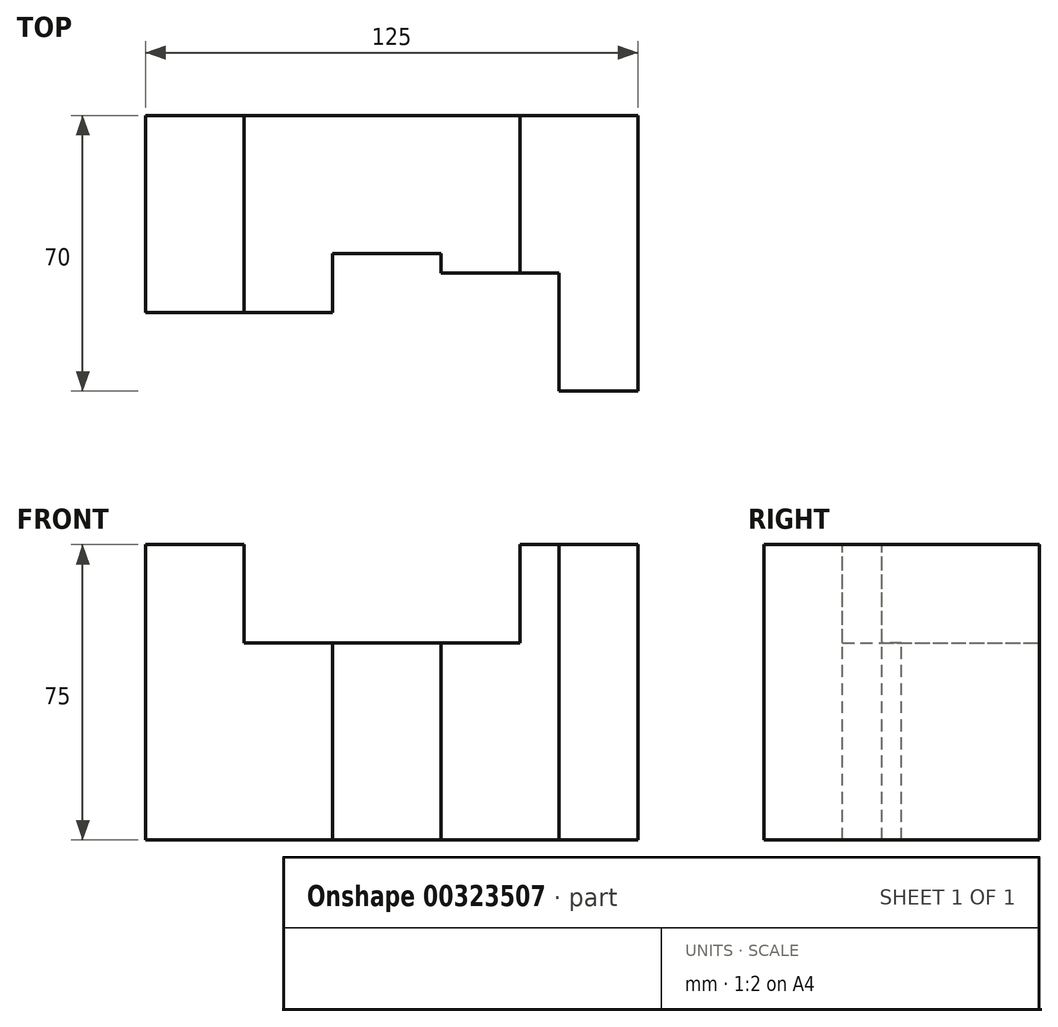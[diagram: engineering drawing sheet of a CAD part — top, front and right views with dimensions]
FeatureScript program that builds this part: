
annotation { "Feature Type Name" : "Feature", "Feature Type Description" : "" }
export const myFeature = defineFeature(function(context is Context, id is Id, definition is map)
    precondition{}
    {
        {
            var Q0;
            Q0=qCreatedBy(makeId("Front.planeOp"),FACE);
            var sketch = newSketch(context, id + "F0", { "sketchPlane" : qUnion([Q0])});
            skLineSegment(sketch, "E0.bottom", {"start": v(-62.5, 75) * mm, "end": v(62.5, 75) * mm});
            skLineSegment(sketch, "E0.top", {"start": v(-62.5, 0) * mm, "end": v(62.5, 0) * mm});
            skLineSegment(sketch, "E0.left", {"start": v(-62.5, 75) * mm, "end": v(-62.5, 0) * mm});
            skLineSegment(sketch, "E0.right", {"start": v(62.5, 75) * mm, "end": v(62.5, 0) * mm});
            skSolve(sketch);
        }
        {
            var Q0;
            Q0 = qSketchRegion(id + "F0", true);
            extrude(context, id + "F1", {"entities" : qUnion([Q0]), "endBound" : BoundingType.SYMMETRIC, "depth" : 70 * mm});
        }
        {
            var Q0;
            Q0=makeQuery(id+"F1.opExtrude","SWEPT_FACE",FACE,{"disambiguationData":[OSD([sQuery(id+"F0.wireOp",EDGE,"E0.bottom")])]});
            var sketch = newSketch(context, id + "F2", { "sketchPlane" : qUnion([Q0])});
            skLineSegment(sketch, "E1", {"start": v(-62.5, -35) * mm, "end": v(-62.5, -15) * mm});
            skLineSegment(sketch, "E2", {"start": v(-62.5, -15) * mm, "end": v(-15, -15) * mm});
            skLineSegment(sketch, "E3", {"start": v(-15, -15) * mm, "end": v(-15, 0) * mm});
            skLineSegment(sketch, "E4", {"start": v(-15, 0) * mm, "end": v(12.5, 0) * mm});
            skLineSegment(sketch, "E5", {"start": v(12.5, 0) * mm, "end": v(12.5, 0) * mm});
            skLineSegment(sketch, "E6", {"start": v(42.5, -5) * mm, "end": v(42.5, -35) * mm});
            skLineSegment(sketch, "E7", {"start": v(42.5, -35) * mm, "end": v(-62.5, -35) * mm});
            skLineSegment(sketch, "E8", {"start": v(12.5, 0) * mm, "end": v(12.5, -5) * mm});
            skLineSegment(sketch, "E9", {"start": v(12.5, -5) * mm, "end": v(42.5, -5) * mm});
            skSolve(sketch);
        }
        {
            var Q0;
            Q0 = qSketchRegion(id + "F2", true);
            extrude(context, id + "F3", {"entities" : qUnion([Q0]), "operationType" : NewBodyOperationType.REMOVE, "endBound" : BoundingType.THROUGH_ALL, "oppositeDirection" : true, "depth" : 25 * mm});
        }
        {
            var Q0;
            Q0=makeQuery(id+"F1.opExtrude","CAP_FACE",FACE,{"disambiguationData":[OSD([sQuery(id+"F0.wireOp",EDGE,"E0.bottom"),sQuery(id+"F0.wireOp",EDGE,"E0.top"),sQuery(id+"F0.wireOp",EDGE,"E0.left"),sQuery(id+"F0.wireOp",EDGE,"E0.right")])],"isStart":true});
            var sketch = newSketch(context, id + "F4", { "sketchPlane" : qUnion([Q0])});
            skLineSegment(sketch, "E10.bottom", {"start": v(-32.5, 75) * mm, "end": v(37.5, 75) * mm});
            skLineSegment(sketch, "E10.top", {"start": v(-32.5, 50) * mm, "end": v(37.5, 50) * mm});
            skLineSegment(sketch, "E10.left", {"start": v(-32.5, 75) * mm, "end": v(-32.5, 50) * mm});
            skLineSegment(sketch, "E10.right", {"start": v(37.5, 75) * mm, "end": v(37.5, 50) * mm});
            skSolve(sketch);
        }
        {
            var Q0;
            Q0 = qSketchRegion(id + "F4", true);
            extrude(context, id + "F5", {"entities" : qUnion([Q0]), "operationType" : NewBodyOperationType.REMOVE, "endBound" : BoundingType.THROUGH_ALL, "oppositeDirection" : true, "depth" : 25 * mm});
        }
    });
